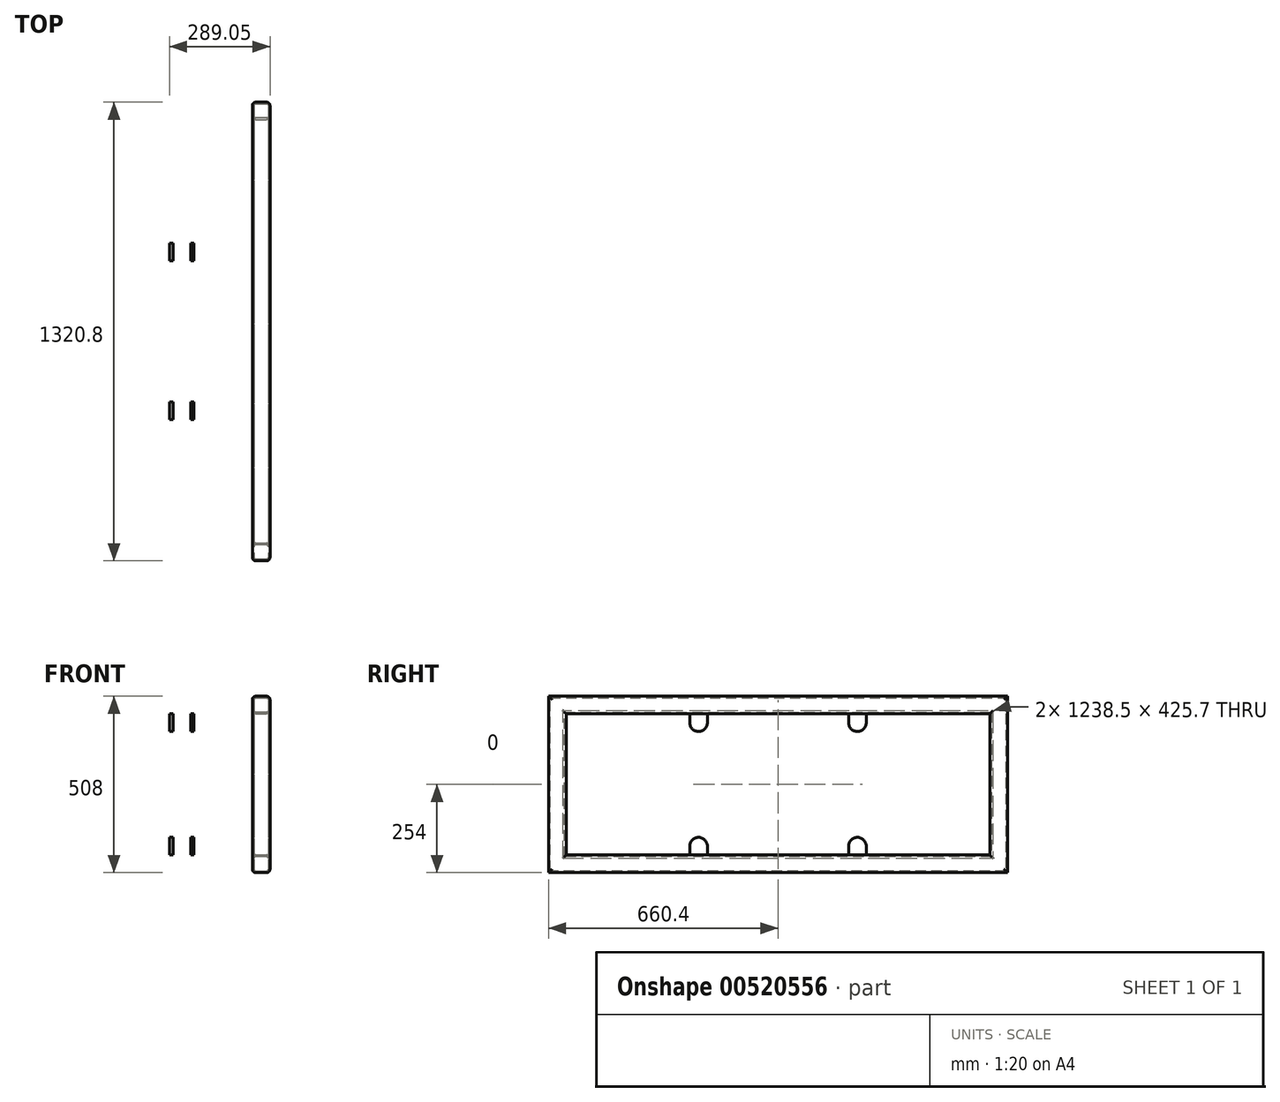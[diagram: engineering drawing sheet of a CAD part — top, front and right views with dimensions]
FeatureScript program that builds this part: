
annotation { "Feature Type Name" : "Feature", "Feature Type Description" : "" }
export const myFeature = defineFeature(function(context is Context, id is Id, definition is map)
    precondition{}
    {
        {
            var Q0;
            Q0=qCreatedBy(makeId("Right.planeOp"),FACE);
            var sketch = newSketch(context, id + "F0", { "sketchPlane" : qUnion([Q0])});
            skLineSegment(sketch, "E0.bottom", {"start": v(-660.4, 254) * mm, "end": v(660.4, 254) * mm});
            skLineSegment(sketch, "E0.top", {"start": v(-660.4, -254) * mm, "end": v(660.4, -254) * mm});
            skLineSegment(sketch, "E0.left", {"start": v(-660.4, 254) * mm, "end": v(-660.4, -254) * mm});
            skLineSegment(sketch, "E0.right", {"start": v(660.4, 254) * mm, "end": v(660.4, -254) * mm});
            skPoint(sketch, "E0.middle", {"position": v(0, 0) * mm});
            skSolve(sketch);
        }
        {
            var Q0;
            Q0=qCreatedBy(makeId("Front.planeOp"),FACE);
            var sketch = newSketch(context, id + "F1", { "sketchPlane" : qUnion([Q0])});
            skPoint(sketch, "E1", {"position": v(0, -254) * mm});
            skLineSegment(sketch, "E2", {"start": v(0, -254) * mm, "end": v(15.75, -254) * mm});
            skLineSegment(sketch, "E3", {"start": v(25.4, -244.35) * mm, "end": v(25.4, -212.85) * mm});
            skLineSegment(sketch, "E4", {"start": v(15.75, -203.2) * mm, "end": v(-15.75, -203.2) * mm});
            skLineSegment(sketch, "E5", {"start": v(-25.4, -212.85) * mm, "end": v(-25.4, -244.35) * mm});
            skLineSegment(sketch, "E6", {"start": v(-15.75, -254) * mm, "end": v(0, -254) * mm});
            skPoint(sketch, "E7.visualSharp", {"position": v(25.4, -254) * mm});
            skArc(sketch, "E7.filletArc", {"start": v(15.75, -254) * mm, "mid": v(22.57, -251.17) * mm, "end": v(25.4, -244.35) * mm});
            skPoint(sketch, "E8.visualSharp", {"position": v(25.4, -203.2) * mm});
            skArc(sketch, "E8.filletArc", {"start": v(25.4, -212.85) * mm, "mid": v(22.57, -206.03) * mm, "end": v(15.75, -203.2) * mm});
            skPoint(sketch, "E9.visualSharp", {"position": v(-25.4, -203.2) * mm});
            skArc(sketch, "E9.filletArc", {"start": v(-15.75, -203.2) * mm, "mid": v(-22.57, -206.03) * mm, "end": v(-25.4, -212.85) * mm});
            skPoint(sketch, "E10.visualSharp", {"position": v(-25.4, -254) * mm});
            skArc(sketch, "E10.filletArc", {"start": v(-25.4, -244.35) * mm, "mid": v(-22.57, -251.17) * mm, "end": v(-15.75, -254) * mm});
            skArc(sketch, "E11.0", {"start": v(15.75, -249.17) * mm, "mid": v(19.16, -247.76) * mm, "end": v(20.57, -244.35) * mm});
            skLineSegment(sketch, "E11.1", {"start": v(0, -249.17) * mm, "end": v(15.75, -249.17) * mm});
            skLineSegment(sketch, "E11.2", {"start": v(20.57, -244.35) * mm, "end": v(20.57, -212.85) * mm});
            skLineSegment(sketch, "E11.3", {"start": v(-15.75, -249.17) * mm, "end": v(0, -249.17) * mm});
            skArc(sketch, "E11.4", {"start": v(-20.57, -244.35) * mm, "mid": v(-19.16, -247.76) * mm, "end": v(-15.75, -249.17) * mm});
            skArc(sketch, "E11.5", {"start": v(20.57, -212.85) * mm, "mid": v(19.16, -209.44) * mm, "end": v(15.75, -208.03) * mm});
            skLineSegment(sketch, "E11.6", {"start": v(15.75, -208.03) * mm, "end": v(-15.75, -208.03) * mm});
            skArc(sketch, "E11.7", {"start": v(-15.75, -208.03) * mm, "mid": v(-19.16, -209.44) * mm, "end": v(-20.57, -212.85) * mm});
            skLineSegment(sketch, "E11.8", {"start": v(-20.57, -212.85) * mm, "end": v(-20.57, -244.35) * mm});
            skSolve(sketch);
        }
        {
            var Q0;
            Q0=makeQuery(id+"F1.imprint","IMPRINT",FACE,{"disambiguationData":[TD([[makeQuery(id+"F1.imprint","IMPRINT",EDGE,{"derivedFrom":sQuery(id+"F1.wireOp",EDGE,"E2")}),1.0]])]});
            var Q1;
            Q1=sQuery(id+"F0.wireOp",EDGE,"E0.top");
            var Q2;
            Q2=sQuery(id+"F0.wireOp",EDGE,"E0.left");
            var Q3;
            Q3=sQuery(id+"F0.wireOp",EDGE,"E0.bottom");
            var Q4;
            Q4=sQuery(id+"F0.wireOp",EDGE,"E0.right");
            sweep(context, id + "F2", {"profiles" : qUnion([Q0]), "path" : qUnion([Q1, Q2, Q3, Q4])});
        }
        {
            var Q0;
            Q0=makeQuery(id+"F2.opSweep","SWEPT_FACE",FACE,{"disambiguationData":[OSD([sQuery(id+"F0.wireOp",EDGE,"E0.top"),sQuery(id+"F1.wireOp",EDGE,"E3")])]});
            var sketch = newSketch(context, id + "F3", { "sketchPlane" : qUnion([Q0])});
            skLineSegment(sketch, "E12", {"start": v(0, 373.49) * mm, "end": v(0, -343.17) * mm, "construction": true});
            skPoint(sketch, "E12.endSnap0", {"position": v(0, -212.85) * mm});
            skLineSegment(sketch, "E13.0", {"start": v(-203.2, 373.49) * mm, "end": v(-203.2, -343.17) * mm, "construction": true});
            skLineSegment(sketch, "E14.0", {"start": v(-660.4, 254) * mm, "end": v(660.4, 254) * mm, "construction": true});
            skLineSegment(sketch, "E15.0", {"start": v(-609.6, 203.2) * mm, "end": v(609.6, 203.2) * mm, "construction": true});
            skLineSegment(sketch, "E16.bottom", {"start": v(-203.2, 254) * mm, "end": v(-193.55, 254) * mm});
            skLineSegment(sketch, "E16.top", {"start": v(-203.2, 203.2) * mm, "end": v(-193.55, 203.2) * mm});
            skLineSegment(sketch, "E16.left", {"start": v(-203.2, 254) * mm, "end": v(-203.2, 203.2) * mm});
            skLineSegment(sketch, "E16.right", {"start": v(-193.55, 254) * mm, "end": v(-193.55, 203.2) * mm});
            skSolve(sketch);
        }
        {
            var Q0;
            Q0 = qSketchRegion(id + "F3", true);
            extrude(context, id + "F4", {"entities" : qUnion([Q0]), "depth" : 50.8 * mm, "offsetDistance" : 25.4 * mm});
        }
        {
            var Q0;
            Q0=makeQuery(id+"F4.opExtrude","CAP_EDGE",EDGE,{"disambiguationData":[OSD([sQuery(id+"F3.wireOp",EDGE,"E16.bottom")])],"isStart":false});
            var Q1;
            Q1=makeQuery(id+"F4.opExtrude","CAP_EDGE",EDGE,{"disambiguationData":[OSD([sQuery(id+"F3.wireOp",EDGE,"E16.top")])],"isStart":false});
            fillet(context, id + "F5", {"entities" : qUnion([Q0, Q1]), "radius" : 25.4 * mm, "tangentPropagation" : true, "allowEdgeOverflow" : false});
        }
        {
            var Q0;
            Q0=makeQuery(id+"F4.opExtrude","SWEPT_FACE",FACE,{"disambiguationData":[OSD([sQuery(id+"F3.wireOp",EDGE,"E16.right")])]});
            var sketch = newSketch(context, id + "F6", { "sketchPlane" : qUnion([Q0])});
            skLineSegment(sketch, "E17", {"start": v(-25.4, 228.6) * mm, "end": v(-50.8, 228.6) * mm, "construction": true});
            skPoint(sketch, "E18", {"position": v(-50.8, 228.6) * mm});
            skSolve(sketch);
        }
        {
            var Q0;
            Q0=sQuery(id+"F6.wireOp",VERTEX,"E18");
            var Q1;
            Q1=makeQuery(id+"F4.opExtrude","SWEPT_BODY",BODY,{"disambiguationData":[OSD([sQuery(id+"F3.wireOp",EDGE,"E16.bottom"),sQuery(id+"F3.wireOp",EDGE,"E16.top"),sQuery(id+"F3.wireOp",EDGE,"E16.left"),sQuery(id+"F3.wireOp",EDGE,"E16.right")])]});
            hole(context, id + "F7", {"style" : HoleStyle.SIMPLE, "endStyle" : HoleEndStyle.THROUGH, "holeDiameter" : 11.18 * mm, "isTappedThrough" : true, "tappedDepth" : 24.82 * mm, "tapClearance" : 3, "locations" : qUnion([Q0]), "scope" : qUnion([Q1])});
        }
        {
            var Q0;
            Q0=makeQuery(id+"F4.opExtrude","SWEPT_FACE",FACE,{"disambiguationData":[OSD([sQuery(id+"F3.wireOp",EDGE,"E16.left")])]});
            cPlane(context, id + "F8", {"entities" : qUnion([Q0]), "cplaneType" : CPlaneType.OFFSET, "offset" : 25.4 * mm, "width" : 152.4 * mm, "height" : 152.4 * mm});
        }
        {
            var Q0;
            Q0=makeQuery(id+"F4.opExtrude","SWEPT_BODY",BODY,{"disambiguationData":[OSD([sQuery(id+"F3.wireOp",EDGE,"E16.bottom"),sQuery(id+"F3.wireOp",EDGE,"E16.top"),sQuery(id+"F3.wireOp",EDGE,"E16.left"),sQuery(id+"F3.wireOp",EDGE,"E16.right")])]});
            var Q1;
            Q1=qCreatedBy(id+"F8.planeOp",FACE);
            mirror(context, id + "F9", {"entities" : qUnion([Q0]), "mirrorPlane" : qUnion([Q1])});
        }
        {
            var Q0;
            Q0=makeQuery(id+"F4.opExtrude","SWEPT_BODY",BODY,{"disambiguationData":[OSD([sQuery(id+"F3.wireOp",EDGE,"E16.bottom"),sQuery(id+"F3.wireOp",EDGE,"E16.top"),sQuery(id+"F3.wireOp",EDGE,"E16.left"),sQuery(id+"F3.wireOp",EDGE,"E16.right")])]});
            var Q1;
            Q1=makeQuery(id+"F9.opPattern","COPY",BODY,{"derivedFrom":makeQuery(id+"F4.opExtrude","SWEPT_BODY",BODY,{"disambiguationData":[OSD([sQuery(id+"F3.wireOp",EDGE,"E16.bottom"),sQuery(id+"F3.wireOp",EDGE,"E16.top"),sQuery(id+"F3.wireOp",EDGE,"E16.left"),sQuery(id+"F3.wireOp",EDGE,"E16.right")])]}),"instanceName":"1"});
            var Q2;
            Q2=qCreatedBy(makeId("Front.planeOp"),FACE);
            mirror(context, id + "F10", {"entities" : qUnion([Q0, Q1]), "mirrorPlane" : qUnion([Q2])});
        }
        {
            var Q0;
            Q0=makeQuery(id+"F9.opPattern","COPY",BODY,{"derivedFrom":makeQuery(id+"F4.opExtrude","SWEPT_BODY",BODY,{"disambiguationData":[OSD([sQuery(id+"F3.wireOp",EDGE,"E16.bottom"),sQuery(id+"F3.wireOp",EDGE,"E16.top"),sQuery(id+"F3.wireOp",EDGE,"E16.left"),sQuery(id+"F3.wireOp",EDGE,"E16.right")])]}),"instanceName":"1"});
            var Q1;
            Q1=makeQuery(id+"F4.opExtrude","SWEPT_BODY",BODY,{"disambiguationData":[OSD([sQuery(id+"F3.wireOp",EDGE,"E16.bottom"),sQuery(id+"F3.wireOp",EDGE,"E16.top"),sQuery(id+"F3.wireOp",EDGE,"E16.left"),sQuery(id+"F3.wireOp",EDGE,"E16.right")])]});
            var Q2;
            Q2=makeQuery(id+"F10.opPattern","COPY",BODY,{"derivedFrom":makeQuery(id+"F4.opExtrude","SWEPT_BODY",BODY,{"disambiguationData":[OSD([sQuery(id+"F3.wireOp",EDGE,"E16.bottom"),sQuery(id+"F3.wireOp",EDGE,"E16.top"),sQuery(id+"F3.wireOp",EDGE,"E16.left"),sQuery(id+"F3.wireOp",EDGE,"E16.right")])]}),"instanceName":"1"});
            var Q3;
            Q3=makeQuery(id+"F10.opPattern","COPY",BODY,{"derivedFrom":makeQuery(id+"F9.opPattern","COPY",BODY,{"derivedFrom":makeQuery(id+"F4.opExtrude","SWEPT_BODY",BODY,{"disambiguationData":[OSD([sQuery(id+"F3.wireOp",EDGE,"E16.bottom"),sQuery(id+"F3.wireOp",EDGE,"E16.top"),sQuery(id+"F3.wireOp",EDGE,"E16.left"),sQuery(id+"F3.wireOp",EDGE,"E16.right")])]}),"instanceName":"1"}),"instanceName":"1"});
            var Q4;
            Q4=qCreatedBy(makeId("Top.planeOp"),FACE);
            mirror(context, id + "F11", {"operationType" : NewBodyOperationType.ADD, "entities" : qUnion([Q0, Q1, Q2, Q3]), "mirrorPlane" : qUnion([Q4])});
        }
    });
